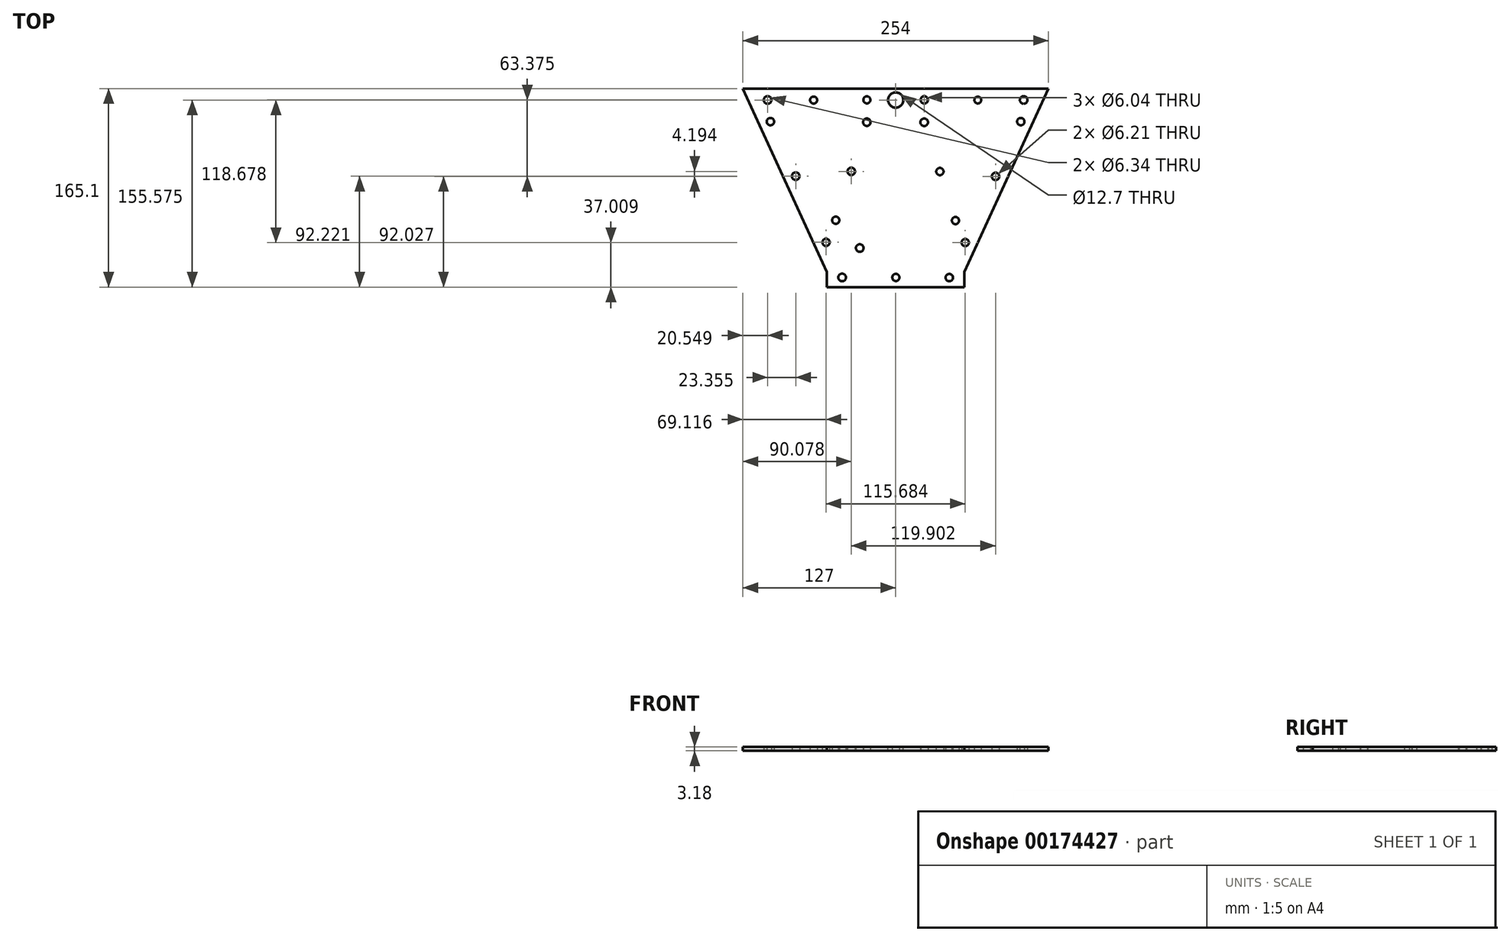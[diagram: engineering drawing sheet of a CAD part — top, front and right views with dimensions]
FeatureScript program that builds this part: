
annotation { "Feature Type Name" : "Feature", "Feature Type Description" : "" }
export const myFeature = defineFeature(function(context is Context, id is Id, definition is map)
    precondition{}
    {
        {
            var Q0;
            Q0=qCreatedBy(makeId("Top.planeOp"),FACE);
            var sketch = newSketch(context, id + "F0", { "sketchPlane" : qUnion([Q0])});
            skLineSegment(sketch, "E0.bottom", {"start": v(101.6, 76.2) * mm, "end": v(-152.4, 76.2) * mm});
            skLineSegment(sketch, "E0.top", {"start": v(31.75, -76.2) * mm, "end": v(-82.55, -76.2) * mm});
            skPoint(sketch, "E0.middle", {"position": v(0, 0) * mm});
            skLineSegment(sketch, "E1", {"start": v(-152.4, 76.2) * mm, "end": v(-82.55, -76.2) * mm});
            skLineSegment(sketch, "E2", {"start": v(101.6, 76.2) * mm, "end": v(31.75, -76.2) * mm});
            skPoint(sketch, "E3.orphan", {"position": v(-101.6, -76.2) * mm});
            skPoint(sketch, "E4.orphan", {"position": v(152.4, -76.2) * mm});
            skLineSegment(sketch, "E5.bottom", {"start": v(-82.55, -76.2) * mm, "end": v(31.75, -76.2) * mm});
            skLineSegment(sketch, "E5.top", {"start": v(-82.55, -88.9) * mm, "end": v(31.75, -88.9) * mm});
            skLineSegment(sketch, "E5.left", {"start": v(-82.55, -76.2) * mm, "end": v(-82.55, -88.9) * mm});
            skLineSegment(sketch, "E5.right", {"start": v(31.75, -76.2) * mm, "end": v(31.75, -88.9) * mm});
            skSolve(sketch);
        }
        {
            var Q0;
            Q0=qSketchRegion(id+"F0",true);
            extrude(context, id + "F1", {"entities" : qUnion([Q0]), "depth" : 3.17 * mm});
        }
        {
            var Q0;
            Q0=makeQuery(id+"F1.opExtrude","CAP_FACE",FACE,{"disambiguationData":[OSD([sQuery(id+"F0.wireOp",EDGE,"E0.bottom"),sQuery(id+"F0.wireOp",EDGE,"E0.top"),sQuery(id+"F0.wireOp",EDGE,"E1"),sQuery(id+"F0.wireOp",EDGE,"E2")])],"isStart":false});
            var sketch = newSketch(context, id + "F2", { "sketchPlane" : qUnion([Q0])});
            skCircle(sketch, "E6", {"center": v(-25.4, 66.67) * mm, "radius": 6.35 * mm});
            skSolve(sketch);
        }
        {
            var Q0;
            Q0=qSketchRegion(id+"F2",true);
            extrude(context, id + "F3", {"entities" : qUnion([Q0]), "operationType" : NewBodyOperationType.REMOVE, "oppositeDirection" : true, "depth" : 25.4 * mm});
        }
        {
            var Q0;
            Q0=makeQuery(id+"F1.opExtrude","CAP_FACE",FACE,{"disambiguationData":[OSD([sQuery(id+"F0.wireOp",EDGE,"E0.bottom"),sQuery(id+"F0.wireOp",EDGE,"E1"),sQuery(id+"F0.wireOp",EDGE,"E2"),sQuery(id+"F0.wireOp",EDGE,"E5.top"),sQuery(id+"F0.wireOp",EDGE,"E5.left"),sQuery(id+"F0.wireOp",EDGE,"E5.right")])],"isStart":true});
            var sketch = newSketch(context, id + "F4", { "sketchPlane" : qUnion([Q0])});
            skCircle(sketch, "E7", {"center": v(-83.28, 51.7) * mm, "radius": 3.02 * mm});
            skCircle(sketch, "E8", {"center": v(-75.22, 33.3) * mm, "radius": 3.03 * mm});
            skCircle(sketch, "E9", {"center": v(-108.5, -3.32) * mm, "radius": 3.17 * mm});
            skCircle(sketch, "E10", {"center": v(-129.5, -48.7) * mm, "radius": 3.07 * mm});
            skCircle(sketch, "E11", {"center": v(-131.85, -66.7) * mm, "radius": 3.17 * mm});
            skCircle(sketch, "E12", {"center": v(-93.6, -66.64) * mm, "radius": 2.93 * mm});
            skCircle(sketch, "E13", {"center": v(-49.32, -66.76) * mm, "radius": 2.95 * mm});
            skCircle(sketch, "E14", {"center": v(-49.38, -48.2) * mm, "radius": 3.1 * mm});
            skCircle(sketch, "E15", {"center": v(-62.32, -7.32) * mm, "radius": 3.1 * mm});
            skCircle(sketch, "E16", {"center": v(-1.62, -66.79) * mm, "radius": 3.02 * mm});
            skCircle(sketch, "E17", {"center": v(42.87, -66.63) * mm, "radius": 2.83 * mm});
            skCircle(sketch, "E18", {"center": v(80.98, -66.7) * mm, "radius": 3.16 * mm});
            skCircle(sketch, "E19", {"center": v(78.6, -48.7) * mm, "radius": 3.04 * mm});
            skCircle(sketch, "E20", {"center": v(-1.71, -48.15) * mm, "radius": 3.14 * mm});
            skCircle(sketch, "E21", {"center": v(11.36, -7.19) * mm, "radius": 3.04 * mm});
            skCircle(sketch, "E22", {"center": v(57.58, -3.13) * mm, "radius": 3.1 * mm});
            skCircle(sketch, "E23", {"center": v(24.3, 33.59) * mm, "radius": 3 * mm});
            skCircle(sketch, "E24", {"center": v(32.4, 51.9) * mm, "radius": 3.02 * mm});
            skSolve(sketch);
        }
        {
            var Q0;
            Q0 = qSketchRegion(id + "F4", true);
            extrude(context, id + "F5", {"entities" : qUnion([Q0]), "operationType" : NewBodyOperationType.REMOVE, "oppositeDirection" : true, "depth" : 25.4 * mm, "offsetDistance" : 25.4 * mm});
        }
        {
            var Q0;
            Q0=makeQuery(id+"F1.opExtrude","CAP_FACE",FACE,{"disambiguationData":[OSD([sQuery(id+"F0.wireOp",EDGE,"E0.bottom"),sQuery(id+"F0.wireOp",EDGE,"E1"),sQuery(id+"F0.wireOp",EDGE,"E2"),sQuery(id+"F0.wireOp",EDGE,"E5.top"),sQuery(id+"F0.wireOp",EDGE,"E5.left"),sQuery(id+"F0.wireOp",EDGE,"E5.right")])],"isStart":true});
            var sketch = newSketch(context, id + "F6", { "sketchPlane" : qUnion([Q0])});
            skCircle(sketch, "E25", {"center": v(-69.92, 80.9) * mm, "radius": 3.19 * mm});
            skCircle(sketch, "E26", {"center": v(-25.26, 80.9) * mm, "radius": 2.98 * mm});
            skCircle(sketch, "E27", {"center": v(19.16, 81.01) * mm, "radius": 3.06 * mm});
            skSolve(sketch);
        }
        {
            var Q0;
            Q0 = qSketchRegion(id + "F6", true);
            extrude(context, id + "F7", {"entities" : qUnion([Q0]), "operationType" : NewBodyOperationType.REMOVE, "oppositeDirection" : true, "depth" : 25.4 * mm, "offsetDistance" : 25.4 * mm});
        }
        {
            var Q0;
            Q0=makeQuery(id+"F1.opExtrude","CAP_FACE",FACE,{"disambiguationData":[OSD([sQuery(id+"F0.wireOp",EDGE,"E0.bottom"),sQuery(id+"F0.wireOp",EDGE,"E1"),sQuery(id+"F0.wireOp",EDGE,"E2"),sQuery(id+"F0.wireOp",EDGE,"E5.top"),sQuery(id+"F0.wireOp",EDGE,"E5.left"),sQuery(id+"F0.wireOp",EDGE,"E5.right")])],"isStart":true});
            var sketch = newSketch(context, id + "F8", { "sketchPlane" : qUnion([Q0])});
            skCircle(sketch, "E28", {"center": v(-55.24, 56.45) * mm, "radius": 3.18 * mm});
            skSolve(sketch);
        }
        {
            var Q0;
            Q0 = qSketchRegion(id + "F8", true);
            extrude(context, id + "F9", {"entities" : qUnion([Q0]), "operationType" : NewBodyOperationType.REMOVE, "oppositeDirection" : true, "depth" : 25.4 * mm, "offsetDistance" : 25.4 * mm});
        }
    });
